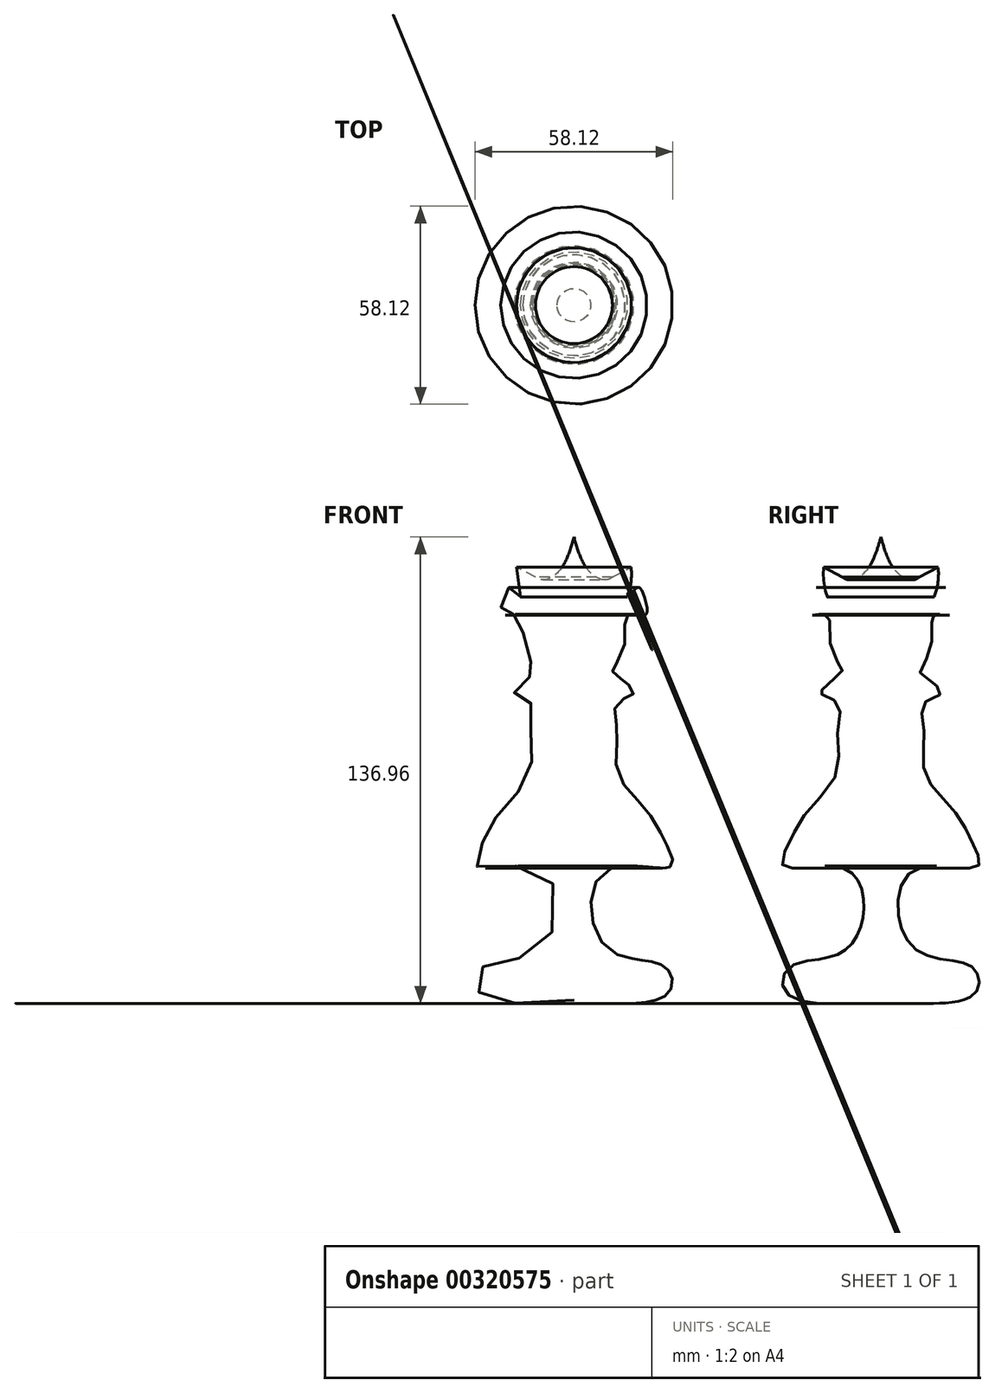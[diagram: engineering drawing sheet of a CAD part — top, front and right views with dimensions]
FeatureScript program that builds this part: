
annotation { "Feature Type Name" : "Feature", "Feature Type Description" : "" }
export const myFeature = defineFeature(function(context is Context, id is Id, definition is map)
    precondition{}
    {
        {
            var Q0;
            Q0=qCreatedBy(makeId("Front.planeOp"),FACE);
            var sketch = newSketch(context, id + "F0", { "sketchPlane" : qUnion([Q0])});
            skFitSpline(sketch, "E0", {"points": [v(0, 65.42) * mm, v(-4.7, 55.07) * mm, v(-11.3, 53.65) * mm, v(-15.53, 61.9) * mm, v(-16.7, 51.77) * mm, v(-15.77, 47.77) * mm, v(-18.83, 50.6) * mm, v(-20.94, 46.83) * mm, v(-20.94, 42.6) * mm, v(-15.77, 42.36) * mm, v(-14.6, 32) * mm, v(-11.3, 26.36) * mm, v(-15.06, 22.83) * mm, v(-17.41, 19.3) * mm, v(-12.7, 16.7) * mm, v(-12.7, 8) * mm, v(-12.94, -4) * mm, v(-21.89, -15.53) * mm, v(-26.83, -24.24) * mm, v(-28.47, -31.3) * mm, v(-8.94, -32.95) * mm, v(-9.41, -55.07) * mm, v(-26.6, -60.71) * mm, v(-27.77, -68.48) * mm, v(0, -70.6) * mm], "startDerivative": vector(-71.27, -252) * mm, "endDerivative": vector(500.23, 43.42) * mm});
            skLineSegment(sketch, "E1", {"start": v(0, 75.54) * mm, "end": v(0, -76) * mm});
            skLineSegment(sketch, "E2", {"start": v(-11.3, 53.65) * mm, "end": v(-16.86, 56.5) * mm});
            skSolve(sketch);
        }
        {
            var Q0;
            {var subQ0=sQuery(id+"F0.wireOp",EDGE,"E0");Q0=makeQuery(id+"F0.imprint","IMPRINT",FACE,{"disambiguationData":[TD([[makeQuery(id+"F0.imprint","IMPRINT",EDGE,{"derivedFrom":subQ0}),1.0]])]});}
            var Q1;
            Q1=sQuery(id+"F0.wireOp",EDGE,"E1");
            revolve(context, id + "F1", {"entities" : qUnion([Q0]), "axis" : qUnion([Q1]), "revolveType" : RevolveType.FULL});
        }
    });
